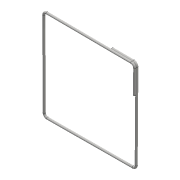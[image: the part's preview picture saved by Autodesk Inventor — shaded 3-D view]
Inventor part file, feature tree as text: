
AUTODESK INVENTOR PART (.ipt)
format: ipt  version: 2016 (Build 200138000, 138)  size: 354,816 bytes
history: native  units: mm
features: sketch x4, plane x3, other x3, sweep x1, helix x1
ambient origin geometry x8: Origin, YZ Plane, XZ Plane, XY Plane, X Axis, Y Axis, Z Axis, Center Point
bodies: Solid1 (feature_tree)
feature tree (12):
  sketch  "Sketch2"  dims[d7=-105.0mm d8=-105.0mm d9=7.5mm]
  plane  "Work Plane1"
  other  "Work Axis1"
  sweep  "Sweep1"
  plane  "Work Plane2"
  plane  "Work Plane3"
  sketch  "Sketch4"  dims[d10=200.0mm]
  other  "Srf1"
  sketch  "3D Sketch3"
  sketch  "Sketch5"  dims[d11=200.0mm d12=50.0mm d17=5.0mm d18=10.0mm d19=11.2mm d20=0.0mm d21=90.0deg d22=90.0deg d23=0.0mm d24=0.0mm d25=120.0mm d26=5.0mm d27=0.0mm d28=0.0mm]
  helix  "Coil1"  [1 undecoded]
  other  "3D Intersection1"
note: 1 required parameter value undecoded (feature->parameter linkage not recoverable at this tier; creation-order binding heuristic only, values carry confidence <= 0.55)
